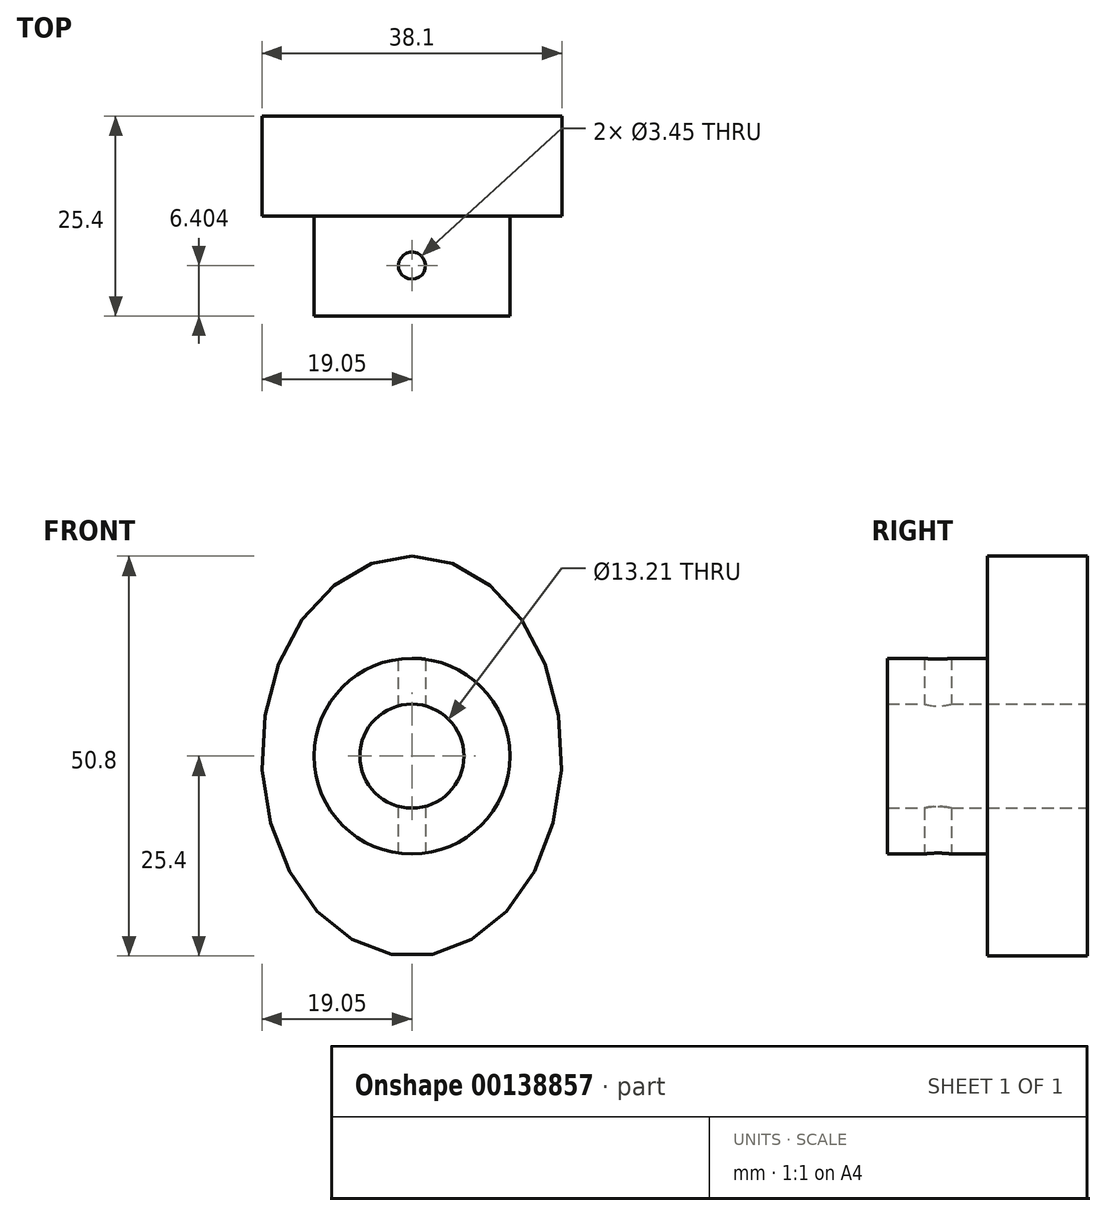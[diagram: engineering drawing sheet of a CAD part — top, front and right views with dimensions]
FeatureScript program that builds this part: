
annotation { "Feature Type Name" : "Feature", "Feature Type Description" : "" }
export const myFeature = defineFeature(function(context is Context, id is Id, definition is map)
    precondition{}
    {
        {
            var Q0;
            Q0=qCreatedBy(makeId("Front.planeOp"),FACE);
            var sketch = newSketch(context, id + "F0", { "sketchPlane" : qUnion([Q0])});
            skEllipse(sketch, "E0", {"center": v(0, 0) * mm, "majorRadius": 25.4 * mm, "minorRadius": 19.05 * mm, "majorAxis": v(0, 1)});
            skLineSegment(sketch, "E1", {"start": v(0, 25.4) * mm, "end": v(29.98, 25.4) * mm, "construction": true});
            skSolve(sketch);
        }
        {
            var Q0;
            Q0=makeQuery(id+"F0.imprint","IMPRINT",FACE,{"disambiguationData":[TD([[makeQuery(id+"F0.imprint","IMPRINT",EDGE,{"derivedFrom":sQuery(id+"F0.wireOp",EDGE,"E0")}),1.0]])]});
            extrude(context, id + "F1", {"entities" : qUnion([Q0]), "depth" : 12.7 * mm});
        }
        {
            var Q0;
            Q0=makeQuery(id+"F1.opExtrude","CAP_FACE",FACE,{"disambiguationData":[OSD([sQuery(id+"F0.wireOp",EDGE,"E0")])],"isStart":false});
            var sketch = newSketch(context, id + "F2", { "sketchPlane" : qUnion([Q0])});
            skCircle(sketch, "E2", {"center": v(0, 0) * mm, "radius": 6.6 * mm});
            skSolve(sketch);
        }
        {
            var Q0;
            Q0=makeQuery(id+"F2.imprint","IMPRINT",FACE,{"disambiguationData":[TD([[makeQuery(id+"F2.imprint","IMPRINT",EDGE,{"derivedFrom":sQuery(id+"F2.wireOp",EDGE,"E2")}),1.0]])]});
            var Q1;
            Q1=sQuery(id+"F2.wireOp",EDGE,"E2");
            extrude(context, id + "F3", {"entities" : qUnion([Q0]), "operationType" : NewBodyOperationType.REMOVE, "surfaceEntities" : qUnion([Q1]), "endBound" : BoundingType.SYMMETRIC, "depth" : 25.4 * mm});
        }
        {
            var Q0;
            Q0=makeQuery(id+"F1.opExtrude","CAP_FACE",FACE,{"disambiguationData":[OSD([sQuery(id+"F0.wireOp",EDGE,"E0")])],"isStart":false});
            var sketch = newSketch(context, id + "F4", { "sketchPlane" : qUnion([Q0])});
            skCircle(sketch, "E3", {"center": v(0, 0) * mm, "radius": 12.44 * mm});
            skSolve(sketch);
        }
        {
            var Q0;
            Q0=makeQuery(id+"F4.imprint","IMPRINT",FACE,{"disambiguationData":[TD([[makeQuery(id+"F4.imprint","IMPRINT",EDGE,{"derivedFrom":sQuery(id+"F4.wireOp",EDGE,"E3")}),1.0]])]});
            extrude(context, id + "F5", {"entities" : qUnion([Q0]), "operationType" : NewBodyOperationType.ADD, "depth" : 12.7 * mm});
        }
        {
            var Q0;
            Q0=qCreatedBy(makeId("Top.planeOp"),FACE);
            var sketch = newSketch(context, id + "F6", { "sketchPlane" : qUnion([Q0])});
            skPoint(sketch, "E4", {"position": v(0, -19) * mm});
            skCircle(sketch, "E5", {"center": v(0, -19) * mm, "radius": 1.73 * mm});
            skLineSegment(sketch, "E6", {"start": v(0, -12.7) * mm, "end": v(0, -25.3) * mm});
            skSolve(sketch);
        }
        {
            var Q0;
            Q0 = qSketchRegion(id + "F6", true);
            var Q1;
            Q1=sQuery(id+"F6.wireOp",EDGE,"E5");
            extrude(context, id + "F7", {"entities" : qUnion([Q0]), "operationType" : NewBodyOperationType.REMOVE, "surfaceEntities" : qUnion([Q1]), "endBound" : BoundingType.SYMMETRIC, "depth" : 25.4 * mm});
        }
    });
